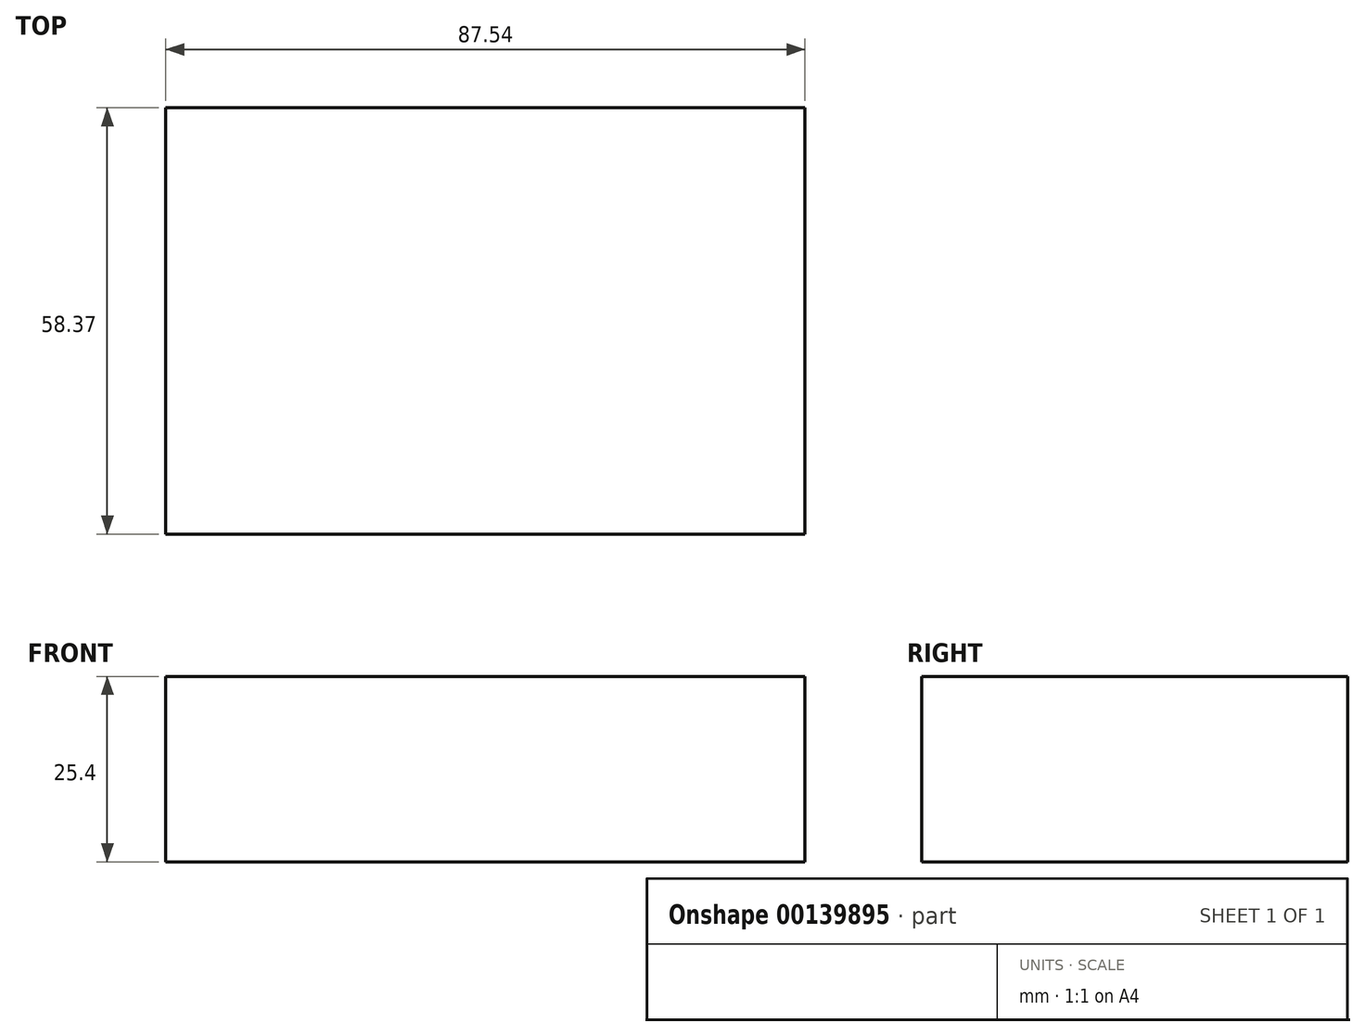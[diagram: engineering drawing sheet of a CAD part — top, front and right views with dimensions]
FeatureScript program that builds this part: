
annotation { "Feature Type Name" : "Feature", "Feature Type Description" : "" }
export const myFeature = defineFeature(function(context is Context, id is Id, definition is map)
    precondition{}
    {
        {
            var Q0;
            Q0=qCreatedBy(makeId("Top.planeOp"),FACE);
            var sketch = newSketch(context, id + "F0", { "sketchPlane" : qUnion([Q0])});
            skLineSegment(sketch, "E0.bottom", {"start": v(-130.84, 25.64) * mm, "end": v(-43.3, 25.64) * mm});
            skLineSegment(sketch, "E0.top", {"start": v(-130.84, -32.73) * mm, "end": v(-43.3, -32.73) * mm});
            skLineSegment(sketch, "E0.left", {"start": v(-130.84, 25.64) * mm, "end": v(-130.84, -32.73) * mm});
            skLineSegment(sketch, "E0.right", {"start": v(-43.3, 25.64) * mm, "end": v(-43.3, -32.73) * mm});
            skSolve(sketch);
        }
        {
            var Q0;
            Q0=makeQuery(id+"F0.imprint","IMPRINT",FACE,{"disambiguationData":[TD([[makeQuery(id+"F0.imprint","IMPRINT",EDGE,{"derivedFrom":sQuery(id+"F0.wireOp",EDGE,"E0.bottom")}),-1.0]])]});
            extrude(context, id + "F1", {"entities" : qUnion([Q0]), "depth" : 25.4 * mm});
        }
    });
